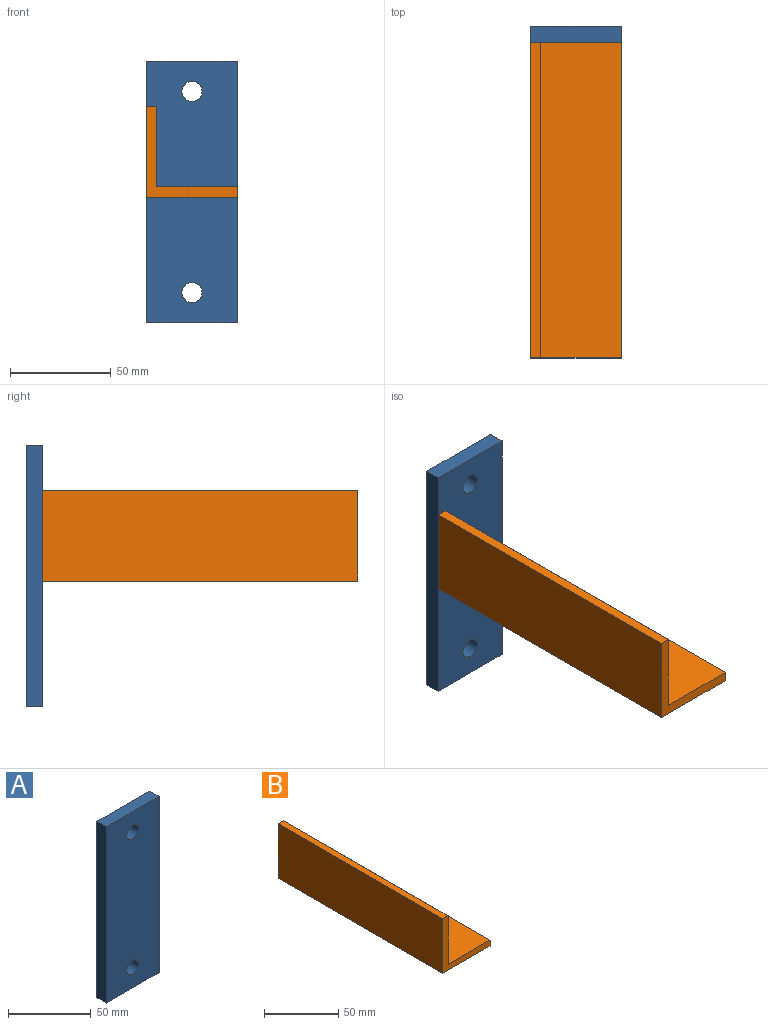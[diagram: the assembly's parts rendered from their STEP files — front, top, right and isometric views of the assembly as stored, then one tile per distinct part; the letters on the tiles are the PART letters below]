
ASSEMBLY  parts=2 mates=1
PART A: 8 faces, bbox 45x8x130 mm
  f0: plane 45x8mm, normal (0,0,-1), area 360mm2, adj f1,f5,f6,f7
  f1: plane 130x8mm, normal (1,0,0), area 1040mm2, adj f0,f2,f6,f7
  f2: plane 45x8mm, normal (0,0,1), area 360mm2, adj f1,f5,f6,f7
  f3: cylinder r=5mm len=10mm, axis (0,1,0), area 251.3mm2, adj f6,f7
  f4: cylinder r=5mm len=10mm, axis (0,1,0), area 251.3mm2, adj f6,f7
  f5: plane 130x8mm, normal (-1,0,0), area 1040mm2, adj f0,f2,f6,f7
  f6: plane 130x45mm, normal (0,-1,0), area 5692.9mm2, adj f0,f1,f2,f3,f4,f5
  f7: plane 130x45mm, normal (0,1,0), area 5692.9mm2, adj f0,f1,f2,f3,f4,f5
PART B: 8 faces, bbox 45x157x45 mm
  f0: plane 157x40mm, normal (0,0,1), area 6280mm2, adj f1,f5,f6,f7
  f1: plane 157x40mm, normal (1,0,0), area 6280mm2, adj f0,f2,f6,f7
  f2: plane 157x5mm, normal (0,0,1), area 785mm2, adj f1,f3,f6,f7
  f3: plane 157x45mm, normal (-1,0,0), area 7065mm2, adj f2,f4,f6,f7
  f4: plane 157x45mm, normal (0,0,-1), area 7065mm2, adj f3,f5,f6,f7
  f5: plane 157x5mm, normal (1,0,0), area 785mm2, adj f0,f4,f6,f7
  f6: plane 45x45mm, normal (0,-1,0), area 425mm2, adj f0,f1,f2,f3,f4,f5
  f7: plane 45x45mm, normal (0,1,0), area 425mm2, adj f0,f1,f2,f3,f4,f5
PLACE A t=(-4.64,-1.53,1.72)mm
PLACE B t=(-27.14,-5.53,-0.78)mm
MATE fastened B.f7 <-> A.f6  axis (0,1,0) through (17.86,-5.53,1.72)mm
